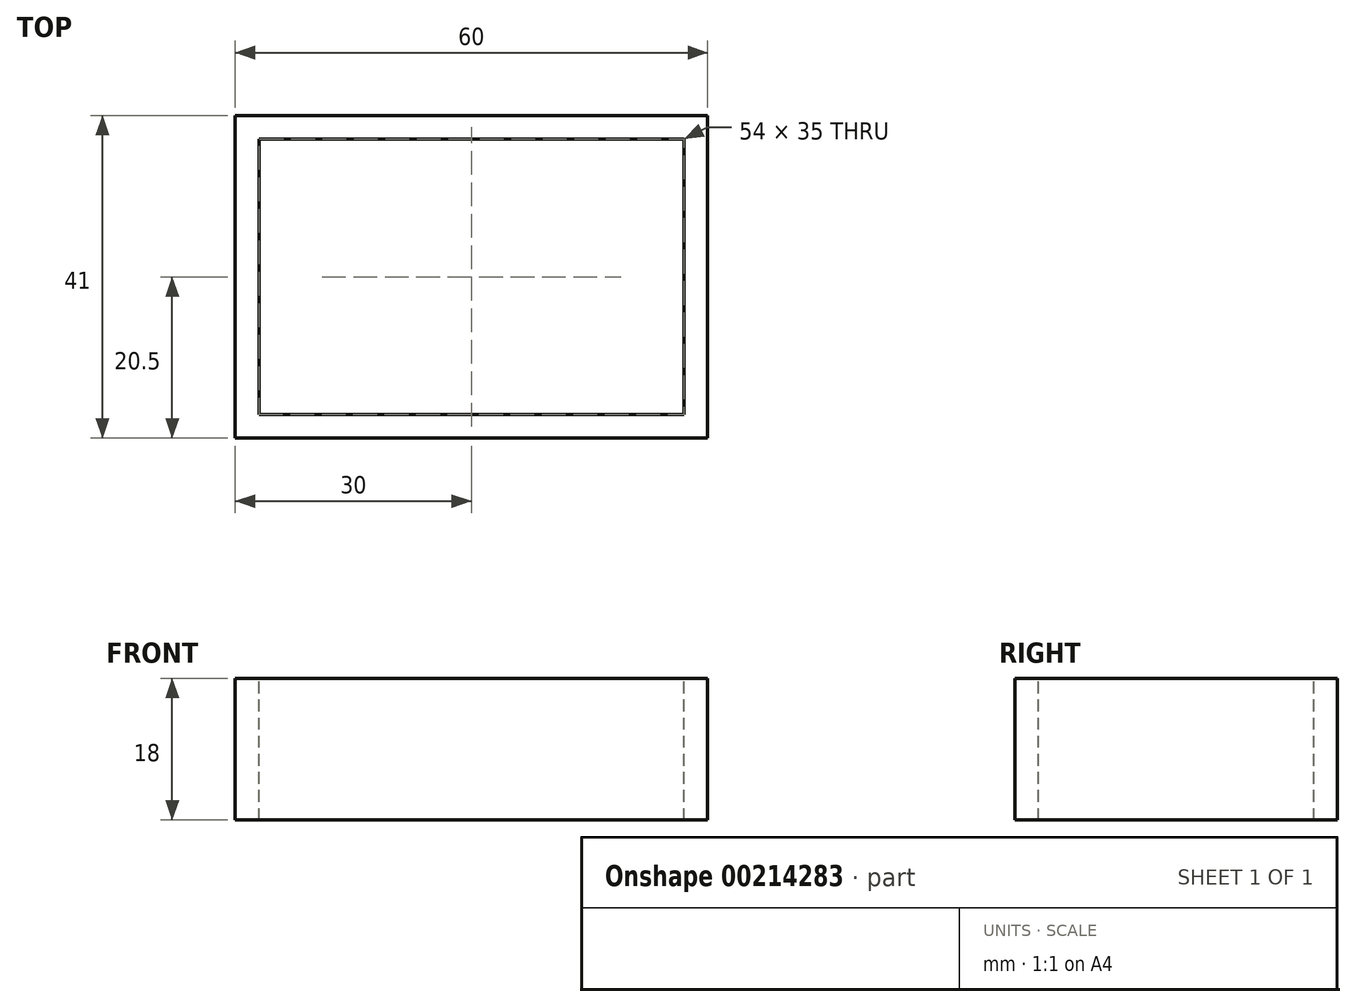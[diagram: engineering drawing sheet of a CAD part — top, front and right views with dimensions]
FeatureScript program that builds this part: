
annotation { "Feature Type Name" : "Feature", "Feature Type Description" : "" }
export const myFeature = defineFeature(function(context is Context, id is Id, definition is map)
    precondition{}
    {
        {
            var Q0;
            Q0=qCreatedBy(makeId("Top.planeOp"),FACE);
            var sketch = newSketch(context, id + "F0", { "sketchPlane" : qUnion([Q0])});
            skLineSegment(sketch, "E0.bottom", {"start": v(-30, 20.5) * mm, "end": v(30, 20.5) * mm});
            skLineSegment(sketch, "E0.top", {"start": v(-30, -20.5) * mm, "end": v(30, -20.5) * mm});
            skLineSegment(sketch, "E0.left", {"start": v(-30, 20.5) * mm, "end": v(-30, -20.5) * mm});
            skLineSegment(sketch, "E0.right", {"start": v(30, 20.5) * mm, "end": v(30, -20.5) * mm});
            skPoint(sketch, "E0.middle", {"position": v(0, 0) * mm});
            skSolve(sketch);
        }
        {
            var Q0;
            Q0 = qSketchRegion(id + "F0", true);
            extrude(context, id + "F1", {"entities" : qUnion([Q0]), "depth" : 18 * mm, "offsetDistance" : 25 * mm});
        }
        {
            var Q0;
            Q0=makeQuery(id+"F1.opExtrude","CAP_FACE",FACE,{"disambiguationData":[OSD([sQuery(id+"F0.wireOp",EDGE,"E0.bottom"),sQuery(id+"F0.wireOp",EDGE,"E0.top"),sQuery(id+"F0.wireOp",EDGE,"E0.left"),sQuery(id+"F0.wireOp",EDGE,"E0.right")])],"isStart":false});
            var sketch = newSketch(context, id + "F2", { "sketchPlane" : qUnion([Q0])});
            skLineSegment(sketch, "E1.bottom", {"start": v(27, -17.5) * mm, "end": v(-27, -17.5) * mm});
            skLineSegment(sketch, "E1.top", {"start": v(27, 17.5) * mm, "end": v(-27, 17.5) * mm});
            skLineSegment(sketch, "E1.left", {"start": v(27, -17.5) * mm, "end": v(27, 17.5) * mm});
            skLineSegment(sketch, "E1.right", {"start": v(-27, -17.5) * mm, "end": v(-27, 17.5) * mm});
            skSolve(sketch);
        }
        {
            var Q0;
            Q0 = qSketchRegion(id + "F2", true);
            extrude(context, id + "F3", {"entities" : qUnion([Q0]), "operationType" : NewBodyOperationType.REMOVE, "oppositeDirection" : true, "depth" : 25 * mm, "offsetDistance" : 25 * mm});
        }
    });
